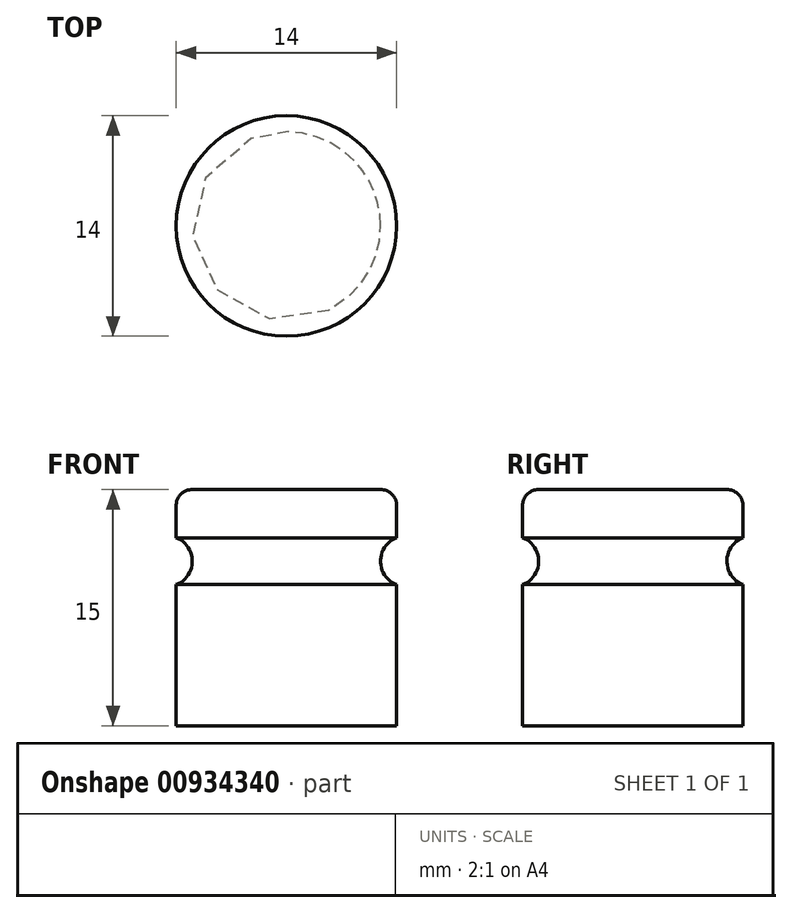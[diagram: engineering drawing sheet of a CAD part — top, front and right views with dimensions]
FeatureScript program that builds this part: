
annotation { "Feature Type Name" : "Feature", "Feature Type Description" : "" }
export const myFeature = defineFeature(function(context is Context, id is Id, definition is map)
    precondition{}
    {
        {
            var Q0;
            Q0=qCreatedBy(makeId("Front.planeOp"),FACE);
            var sketch = newSketch(context, id + "F0", { "sketchPlane" : qUnion([Q0])});
            skLineSegment(sketch, "E0", {"start": v(0, 0) * mm, "end": v(7, 0) * mm});
            skLineSegment(sketch, "E1", {"start": v(7, 0) * mm, "end": v(7, 8.96) * mm});
            skLineSegment(sketch, "E2", {"start": v(7, 15) * mm, "end": v(0, 15) * mm});
            skLineSegment(sketch, "E3.trimOffspring", {"start": v(7, 11.95) * mm, "end": v(7, 15) * mm});
            skArc(sketch, "E4", {"start": v(7, 11.95) * mm, "mid": v(5.98, 10.45) * mm, "end": v(7, 8.96) * mm});
            skLineSegment(sketch, "E5", {"start": v(0, 15) * mm, "end": v(0, 0) * mm});
            skLineSegment(sketch, "E6", {"start": v(0, 17.23) * mm, "end": v(0, -2.96) * mm, "construction": true});
            skSolve(sketch);
        }
        {
            var Q0;
            Q0=makeQuery(id+"F0.imprint","IMPRINT",FACE,{"disambiguationData":[TD([[makeQuery(id+"F0.imprint","IMPRINT",EDGE,{"derivedFrom":sQuery(id+"F0.wireOp",EDGE,"E0")}),1.0]])]});
            var Q1;
            Q1=sQuery(id+"F0.wireOp",EDGE,"E5");
            revolve(context, id + "F1", {"surfaceOperationType" : NewSurfaceOperationType.NEW, "entities" : qUnion([Q0]), "axis" : qUnion([Q1]), "revolveType" : RevolveType.FULL});
        }
        {
            var Q0;
            Q0=makeQuery(id+"F1.opRevolve","SWEPT_EDGE",EDGE,{"disambiguationData":[OSD([sQuery(id+"F0.wireOp",EDGE,"E2"),sQuery(id+"F0.wireOp",EDGE,"E3.trimOffspring")])]});
            fillet(context, id + "F2", {"entities" : qUnion([Q0]), "radius" : 1 * mm, "tangentPropagation" : true, "allowEdgeOverflow" : false});
        }
    });
